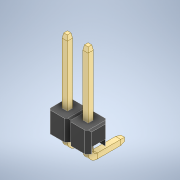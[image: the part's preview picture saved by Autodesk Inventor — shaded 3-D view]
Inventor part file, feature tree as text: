
AUTODESK INVENTOR PART (.ipt)
format: ipt  version: 2021 (Build 250183000, 183)  size: 181,248 bytes
history: native  units: in
note: dims shown in document units (in); Inventor stores cm internally (conversion verified against a paired STEP export)
features: chamfer x1, other x1, boolean_combine x1
ambient origin geometry x8: Origin, YZ Plane, XZ Plane, XY Plane, X Axis, Y Axis, Z Axis, Center Point
bodies: Solid1 (feature_tree), Solid2 (feature_tree), Solid3 (feature_tree)
feature tree (3):
  chamfer  "Chamfer3"  [1 undecoded]
  other  "LPattern1[1]"
  boolean_combine  "Combine1"
note: 1 required parameter value undecoded (feature->parameter linkage not recoverable at this tier; creation-order binding heuristic only, values carry confidence <= 0.55)
